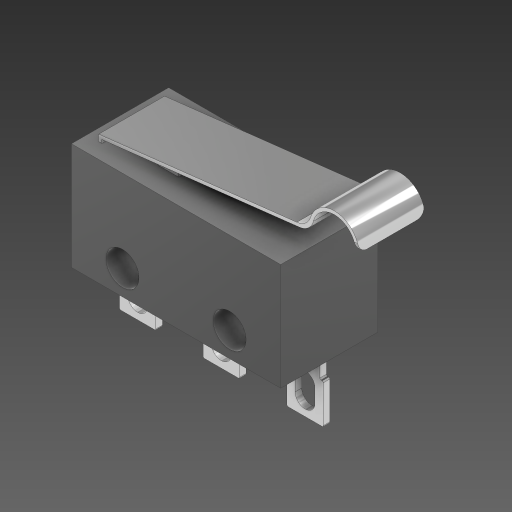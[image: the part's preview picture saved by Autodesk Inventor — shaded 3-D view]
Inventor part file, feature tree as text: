
AUTODESK INVENTOR PART (.ipt)
format: ipt  version: 2024 (Build 280153000, 153)  size: 266,240 bytes
history: native  units: mm
features: extrude x4, sketch x4, fillet x3, plane x1, pattern_linear x1
ambient origin geometry x8: Origin, YZ Plane, XZ Plane, XY Plane, X Axis, Y Axis, Z Axis, Center Point
bodies: Solid1 (feature_tree)
feature tree (13):
  extrude  "Extrusion1"  Depth=6.5mm
  plane  "Work Plane1"
  extrude  "Extrusion2"  Depth=2.0mm
  extrude  "Extrusion3"  Depth=3.25mm
  fillet  "Fillet1"  Radius=6.5mm
  pattern_linear  "Rectangular Pattern1"  Spacing1=2.2mm  [1 undecoded]
  extrude  "Extrusion4"  Depth=0.5mm TaperAngle=0.0deg
  fillet  "Fillet2"  Radius=1.2mm
  fillet  "Fillet3"  Radius=5.2mm
  sketch  "Sketch1"  dims[d0=12.7mm d1=6.5mm]
  sketch  "Sketch2"  dims[d2=2.0mm d3=2.0mm]
  sketch  "Sketch3"  dims[d4=1.5mm d5=3.25mm d6=6.5mm]
  sketch  "Sketch4"  dims[d7=5.9mm d8=0.0mm d13=2.2mm d15=0.4mm d16=0.0mm d17=1.2mm d18=5.2mm d19=2.9mm d20=0.0mm d21=0.8mm d22=0.6mm d23=1.0mm d24=1.8mm d27=5.08mm d28=1.1mm d29=3.5mm d37=0.075mm d38=30.0mm d40=5.08mm d43=15.0mm d44=10.0mm d45=0.2mm d47=0.8mm d49=3.0mm d50=0.2mm d51=0.2mm d52=0.2mm d53=4.0mm d54=0.0mm d55=1.0mm d56=0.5mm]
note: 1 required parameter value undecoded (feature->parameter linkage not recoverable at this tier; creation-order binding heuristic only, values carry confidence <= 0.55)
